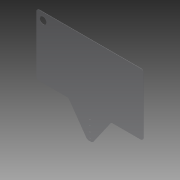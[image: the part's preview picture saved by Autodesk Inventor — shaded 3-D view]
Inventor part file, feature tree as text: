
AUTODESK INVENTOR PART (.ipt)
format: ipt  version: 2014 (Build 180170000, 170)  size: 140,288 bytes
history: native  units: in
note: dims shown in document units (in); Inventor stores cm internally (conversion verified against a paired STEP export)
features: extrude x2, sketch x2, fillet x1
ambient origin geometry x8: Origin, YZ Plane, XZ Plane, XY Plane, X Axis, Y Axis, Z Axis, Center Point
bodies: Solid1 (feature_tree)
feature tree (5):
  extrude  "Extrusion1"  Depth=16.5in
  fillet  "Fillet1"  Radius=16.5in
  extrude  "Extrusion2"  Depth=0.0625in
  sketch  "Sketch1"  dims[d0=1.0in d2=10.0in d3=16.5in]
  sketch  "Sketch2"  dims[d4=5.0in d5=6.0in d6=0.164in d7=0.5in d8=1.5748in d10=1.0in d11=0.3937in d13=1.0in d15=0.0625in d16=0.0in d17=0.5in d18=1.25in d19=1.375in d20=1.25in d21=4.3307in d23=1.75in d24=3.1496in d26=1.75in d29=0.0625in d30=0.0in]
